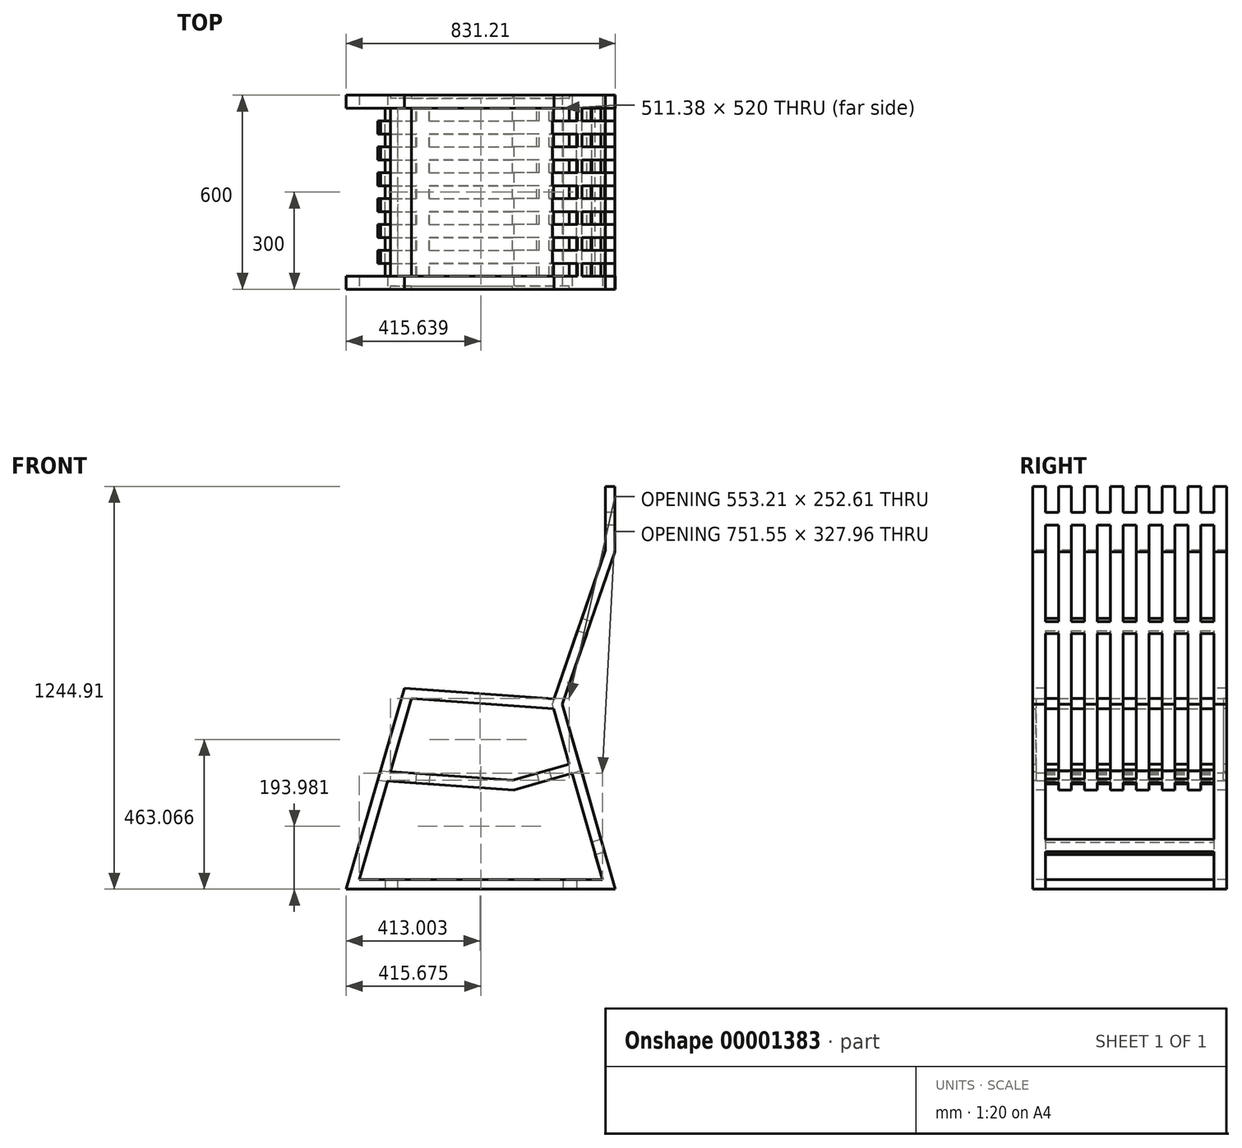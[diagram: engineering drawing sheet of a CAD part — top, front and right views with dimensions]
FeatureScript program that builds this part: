
annotation { "Feature Type Name" : "Feature", "Feature Type Description" : "" }
export const myFeature = defineFeature(function(context is Context, id is Id, definition is map)
    precondition{}
    {
        {
            var Q0;
            Q0=qCreatedBy(makeId("Front.planeOp"),FACE);
            var sketch = newSketch(context, id + "F0", { "sketchPlane" : qUnion([Q0])});
            skLineSegment(sketch, "E0", {"start": v(0, 0) * mm, "end": v(175.03, 605.2) * mm, "construction": true});
            skLineSegment(sketch, "E1", {"start": v(101.23, 350) * mm, "end": v(500.22, 321.6) * mm, "construction": true});
            skLineSegment(sketch, "E2", {"start": v(500.22, 321.6) * mm, "end": v(692.54, 376.5) * mm, "construction": true});
            skLineSegment(sketch, "E3", {"start": v(692.54, 376.5) * mm, "end": v(636.64, 572.35) * mm, "construction": true});
            skLineSegment(sketch, "E4", {"start": v(636.64, 572.35) * mm, "end": v(800, 1044.91) * mm, "construction": true});
            skLineSegment(sketch, "E5", {"start": v(0, 0) * mm, "end": v(800, 0) * mm, "construction": true});
            skLineSegment(sketch, "E6", {"start": v(800, 1044.91) * mm, "end": v(800, 1244.91) * mm, "construction": true});
            skLineSegment(sketch, "E7", {"start": v(636.64, 572.35) * mm, "end": v(175.03, 605.2) * mm, "construction": true});
            skLineSegment(sketch, "E8", {"start": v(815.6, 0) * mm, "end": v(-15.61, 0) * mm});
            skLineSegment(sketch, "E9", {"start": v(800, 1244.91) * mm, "end": v(800, 1044.91) * mm});
            skLineSegment(sketch, "E10.0", {"start": v(785, 1244.91) * mm, "end": v(785, 1044.91) * mm});
            skLineSegment(sketch, "E11.0", {"start": v(815, 1244.91) * mm, "end": v(815, 1044.91) * mm});
            skLineSegment(sketch, "E12.0", {"start": v(785.82, 1049.81) * mm, "end": v(626.22, 588.13) * mm});
            skLineSegment(sketch, "E13.0", {"start": v(815, 1042.4) * mm, "end": v(652.36, 571.92) * mm});
            skLineSegment(sketch, "E13.1", {"start": v(815, 1244.91) * mm, "end": v(815, 1042.4) * mm});
            skLineSegment(sketch, "E14.0", {"start": v(164, 621.02) * mm, "end": v(-15.61, 0) * mm});
            skLineSegment(sketch, "E14.2", {"start": v(815.6, 0) * mm, "end": v(652.36, 571.92) * mm});
            skLineSegment(sketch, "E15.0", {"start": v(682.23, 357.96) * mm, "end": v(501.8, 306.46) * mm});
            skLineSegment(sketch, "E15.1", {"start": v(112.27, 334.18) * mm, "end": v(501.8, 306.46) * mm});
            skLineSegment(sketch, "E16.0", {"start": v(674, 386.8) * mm, "end": v(498.64, 336.76) * mm});
            skLineSegment(sketch, "E16.1", {"start": v(120.79, 363.65) * mm, "end": v(498.64, 336.76) * mm});
            skLineSegment(sketch, "E17.0", {"start": v(775.84, 30) * mm, "end": v(682.23, 357.96) * mm});
            skLineSegment(sketch, "E17.2", {"start": v(186.07, 589.37) * mm, "end": v(120.79, 363.65) * mm});
            skLineSegment(sketch, "E17.3", {"start": v(186.07, 589.37) * mm, "end": v(625.1, 558.13) * mm});
            skLineSegment(sketch, "E18.0", {"start": v(775.84, 30) * mm, "end": v(24.3, 30) * mm});
            skLineSegment(sketch, "E19", {"start": v(785, 1244.91) * mm, "end": v(815, 1244.91) * mm});
            skLineSegment(sketch, "E20", {"start": v(164, 621.02) * mm, "end": v(626.22, 588.13) * mm});
            skLineSegment(sketch, "E21.trimOffspring", {"start": v(112.27, 334.18) * mm, "end": v(24.3, 30) * mm});
            skLineSegment(sketch, "E22.trimOffspring", {"start": v(674, 386.8) * mm, "end": v(625.1, 558.13) * mm});
            skSolve(sketch);
        }
        {
            var Q0;
            Q0 = qSketchRegion(id + "F0", true);
            extrude(context, id + "F1", {"entities" : qUnion([Q0]), "oppositeDirection" : true, "depth" : 30 * mm});
        }
        {
            var Q0;
            Q0=makeQuery(id+"F1.opExtrude","CAP_FACE",FACE,{"disambiguationData":[OSD([sQuery(id+"F0.wireOp",EDGE,"E8"),sQuery(id+"F0.wireOp",EDGE,"E10.0"),sQuery(id+"F0.wireOp",EDGE,"E12.0"),sQuery(id+"F0.wireOp",EDGE,"E13.0"),sQuery(id+"F0.wireOp",EDGE,"E13.1"),sQuery(id+"F0.wireOp",EDGE,"E14.0"),sQuery(id+"F0.wireOp",EDGE,"E14.2"),sQuery(id+"F0.wireOp",EDGE,"E15.0"),sQuery(id+"F0.wireOp",EDGE,"E15.1"),sQuery(id+"F0.wireOp",EDGE,"E16.0"),sQuery(id+"F0.wireOp",EDGE,"E16.1"),sQuery(id+"F0.wireOp",EDGE,"E17.0"),sQuery(id+"F0.wireOp",EDGE,"E17.2"),sQuery(id+"F0.wireOp",EDGE,"E17.3"),sQuery(id+"F0.wireOp",EDGE,"E18.0"),sQuery(id+"F0.wireOp",EDGE,"E19"),sQuery(id+"F0.wireOp",EDGE,"E20"),sQuery(id+"F0.wireOp",EDGE,"E21.trimOffspring"),sQuery(id+"F0.wireOp",EDGE,"E22.trimOffspring")])],"isStart":false});
            var sketch = newSketch(context, id + "F2", { "sketchPlane" : qUnion([Q0])});
            skLineSegment(sketch, "E23.2", {"start": v(-90.19, 365.82) * mm, "end": v(-81.67, 336.35) * mm});
            skLineSegment(sketch, "E24", {"start": v(-652.36, 571.92) * mm, "end": v(-711.08, 366.2) * mm});
            skLineSegment(sketch, "E25", {"start": v(-785, 1244.91) * mm, "end": v(-815, 1244.91) * mm});
            skLineSegment(sketch, "E26", {"start": v(-815, 1244.91) * mm, "end": v(-815, 1042.4) * mm});
            skLineSegment(sketch, "E27", {"start": v(-815, 1042.4) * mm, "end": v(-652.36, 571.92) * mm});
            skLineSegment(sketch, "E28", {"start": v(-785, 1244.91) * mm, "end": v(-785, 1047.43) * mm});
            skLineSegment(sketch, "E29", {"start": v(-785, 1047.43) * mm, "end": v(-626.22, 588.13) * mm});
            skLineSegment(sketch, "E30", {"start": v(-620.92, 572.78) * mm, "end": v(-674, 386.8) * mm});
            skLineSegment(sketch, "E31", {"start": v(-674, 386.8) * mm, "end": v(-498.64, 336.76) * mm});
            skLineSegment(sketch, "E32", {"start": v(-498.64, 336.76) * mm, "end": v(-90.19, 365.82) * mm});
            skLineSegment(sketch, "E33", {"start": v(-711.08, 366.2) * mm, "end": v(-501.8, 306.46) * mm});
            skLineSegment(sketch, "E34", {"start": v(-501.8, 306.46) * mm, "end": v(-81.67, 336.35) * mm});
            skPoint(sketch, "E35.orphan", {"position": v(-164, 621.02) * mm});
            skPoint(sketch, "E36.orphan", {"position": v(15.61, 0) * mm});
            skLineSegment(sketch, "E37", {"start": v(-620.92, 572.78) * mm, "end": v(-626.22, 588.13) * mm});
            skSolve(sketch);
        }
        {
            var Q0;
            {var subQ2=sQuery(id+"F2.wireOp",EDGE,"E23.2");Q0=makeQuery(id+"F2.imprint","IMPRINT",FACE,{"disambiguationData":[TD([[makeQuery(id+"F2.imprint","IMPRINT",EDGE,{"derivedFrom":subQ2}),-1.0]])]});}
            extrude(context, id + "F3", {"entities" : qUnion([Q0]), "operationType" : NewBodyOperationType.ADD, "depth" : 520 * mm});
        }
        {
            var Q0;
            Q0=makeQuery(id+"F3.opExtrude","CAP_FACE",FACE,{"disambiguationData":[OSD([sQuery(id+"F2.wireOp",EDGE,"E23.2"),sQuery(id+"F2.wireOp",EDGE,"E24"),sQuery(id+"F2.wireOp",EDGE,"E25"),sQuery(id+"F2.wireOp",EDGE,"E26"),sQuery(id+"F2.wireOp",EDGE,"E27"),sQuery(id+"F2.wireOp",EDGE,"E28"),sQuery(id+"F2.wireOp",EDGE,"E29"),sQuery(id+"F2.wireOp",EDGE,"E30"),sQuery(id+"F2.wireOp",EDGE,"E31"),sQuery(id+"F2.wireOp",EDGE,"E32"),sQuery(id+"F2.wireOp",EDGE,"E33"),sQuery(id+"F2.wireOp",EDGE,"E34"),sQuery(id+"F2.wireOp",EDGE,"E37")])],"isStart":false});
            var sketch = newSketch(context, id + "F4", { "sketchPlane" : qUnion([Q0])});
            skLineSegment(sketch, "E38", {"start": v(-785, 1244.91) * mm, "end": v(-815, 1244.91) * mm});
            skLineSegment(sketch, "E39", {"start": v(-815, 1244.91) * mm, "end": v(-815, 1042.4) * mm});
            skLineSegment(sketch, "E40", {"start": v(-815, 1042.4) * mm, "end": v(-652.36, 571.92) * mm});
            skLineSegment(sketch, "E41", {"start": v(-652.36, 571.92) * mm, "end": v(-815.6, 0) * mm});
            skLineSegment(sketch, "E42", {"start": v(-785, 1244.91) * mm, "end": v(-785, 1047.43) * mm});
            skLineSegment(sketch, "E43", {"start": v(-785, 1047.43) * mm, "end": v(-626.22, 588.13) * mm});
            skLineSegment(sketch, "E44", {"start": v(-625.1, 558.13) * mm, "end": v(-674, 386.8) * mm});
            skLineSegment(sketch, "E45", {"start": v(-674, 386.8) * mm, "end": v(-498.64, 336.76) * mm});
            skLineSegment(sketch, "E46", {"start": v(-498.64, 336.76) * mm, "end": v(-120.79, 363.65) * mm});
            skLineSegment(sketch, "E47.0", {"start": v(-164, 621.02) * mm, "end": v(15.61, 0) * mm});
            skLineSegment(sketch, "E48.0", {"start": v(-164, 621.02) * mm, "end": v(-626.22, 588.13) * mm});
            skLineSegment(sketch, "E49.0", {"start": v(-186.07, 589.37) * mm, "end": v(-120.79, 363.65) * mm});
            skLineSegment(sketch, "E50.0", {"start": v(-186.07, 589.37) * mm, "end": v(-625.1, 558.13) * mm});
            skLineSegment(sketch, "E51.0", {"start": v(-112.27, 334.18) * mm, "end": v(-501.8, 306.46) * mm});
            skLineSegment(sketch, "E52.0", {"start": v(-682.23, 357.96) * mm, "end": v(-501.8, 306.46) * mm});
            skLineSegment(sketch, "E53.0", {"start": v(-775.84, 30) * mm, "end": v(-682.23, 357.96) * mm});
            skLineSegment(sketch, "E54.0", {"start": v(-775.84, 30) * mm, "end": v(-24.3, 30) * mm});
            skLineSegment(sketch, "E55.0", {"start": v(-112.27, 334.18) * mm, "end": v(-24.3, 30) * mm});
            skLineSegment(sketch, "E56.0", {"start": v(-815.6, 0) * mm, "end": v(15.61, 0) * mm});
            skPoint(sketch, "E57.orphan", {"position": v(-81.67, 336.35) * mm});
            skPoint(sketch, "E58.orphan", {"position": v(-711.08, 366.2) * mm});
            skSolve(sketch);
        }
        {
            var Q0;
            {var subQ8=sQuery(id+"F4.wireOp",EDGE,"E48.0");Q0=makeQuery(id+"F4.imprint","IMPRINT",FACE,{"disambiguationData":[TD([[makeQuery(id+"F4.imprint","IMPRINT",EDGE,{"derivedFrom":subQ8}),1.0]])]});}
            var Q1;
            Q1=makeQuery(id+"F4.imprint","IMPRINT",FACE,{"disambiguationData":[TD([[makeQuery(id+"F4.imprint","IMPRINT",EDGE,{"derivedFrom":sQuery(id+"F4.wireOp",EDGE,"E38")}),1.0]])]});
            var Q2;
            {var subQ1=sQuery(id+"F4.wireOp",EDGE,"E53.0");Q2=makeQuery(id+"F4.imprint","IMPRINT",FACE,{"disambiguationData":[TD([[makeQuery(id+"F4.imprint","IMPRINT",EDGE,{"derivedFrom":subQ1}),1.0]])]});}
            extrude(context, id + "F5", {"entities" : qUnion([Q0, Q1, Q2]), "operationType" : NewBodyOperationType.ADD, "depth" : 30 * mm});
        }
        {
            var Q0;
            Q0=qCreatedBy(makeId("Right.planeOp"),FACE);
            var sketch = newSketch(context, id + "F6", { "sketchPlane" : qUnion([Q0])});
            skPoint(sketch, "E59.0", {"position": v(550, 621.02) * mm});
            skLineSegment(sketch, "E60.0", {"start": v(550, 1244.91) * mm, "end": v(550, 365.82) * mm, "construction": true});
            skLineSegment(sketch, "E61.0", {"start": v(30, 621.02) * mm, "end": v(30, 365.82) * mm, "construction": true});
            skLineSegment(sketch, "E62.0", {"start": v(510, 1244.91) * mm, "end": v(510, 279.99) * mm, "construction": true});
            skLineSegment(sketch, "E63.0", {"start": v(580, 1244.91) * mm, "end": v(0, 1244.91) * mm, "construction": true});
            skLineSegment(sketch, "E64.bottom", {"start": v(550, 1244.91) * mm, "end": v(510, 1244.91) * mm});
            skLineSegment(sketch, "E64.top", {"start": v(550, 279.99) * mm, "end": v(510, 279.99) * mm});
            skLineSegment(sketch, "E64.left", {"start": v(550, 1244.91) * mm, "end": v(550, 279.99) * mm});
            skLineSegment(sketch, "E64.right", {"start": v(510, 1244.91) * mm, "end": v(510, 279.99) * mm});
            skLineSegment(sketch, "E65.0", {"start": v(470, 1244.91) * mm, "end": v(470, 279.99) * mm});
            skLineSegment(sketch, "E66.0", {"start": v(430, 1244.91) * mm, "end": v(430, 279.99) * mm});
            skLineSegment(sketch, "E67.0", {"start": v(390, 1244.91) * mm, "end": v(390, 279.99) * mm});
            skLineSegment(sketch, "E68.0", {"start": v(350, 1244.91) * mm, "end": v(350, 279.99) * mm});
            skLineSegment(sketch, "E69.0", {"start": v(310, 1244.91) * mm, "end": v(310, 279.99) * mm});
            skLineSegment(sketch, "E70.0", {"start": v(270, 1244.91) * mm, "end": v(270, 279.99) * mm});
            skLineSegment(sketch, "E71.0", {"start": v(230, 1244.91) * mm, "end": v(230, 279.99) * mm});
            skLineSegment(sketch, "E72.0", {"start": v(190, 1244.91) * mm, "end": v(190, 279.99) * mm});
            skLineSegment(sketch, "E73.0", {"start": v(150, 1244.91) * mm, "end": v(150, 279.99) * mm});
            skLineSegment(sketch, "E74.0", {"start": v(110, 1244.91) * mm, "end": v(110, 279.99) * mm});
            skLineSegment(sketch, "E75.0", {"start": v(70, 1244.91) * mm, "end": v(70, 279.99) * mm});
            skLineSegment(sketch, "E76.0", {"start": v(30, 1244.91) * mm, "end": v(30, 279.99) * mm});
            skLineSegment(sketch, "E77", {"start": v(470, 279.99) * mm, "end": v(430, 279.99) * mm});
            skLineSegment(sketch, "E78", {"start": v(390, 279.99) * mm, "end": v(350, 279.99) * mm});
            skLineSegment(sketch, "E79", {"start": v(310, 279.99) * mm, "end": v(270, 279.99) * mm});
            skLineSegment(sketch, "E80", {"start": v(230, 279.99) * mm, "end": v(190, 279.99) * mm});
            skLineSegment(sketch, "E81", {"start": v(150, 279.99) * mm, "end": v(110, 279.99) * mm});
            skLineSegment(sketch, "E82", {"start": v(70, 279.99) * mm, "end": v(30, 279.99) * mm});
            skLineSegment(sketch, "E83", {"start": v(470, 1244.91) * mm, "end": v(430, 1244.91) * mm});
            skLineSegment(sketch, "E84", {"start": v(390, 1244.91) * mm, "end": v(350, 1244.91) * mm});
            skLineSegment(sketch, "E85", {"start": v(310, 1244.91) * mm, "end": v(270, 1244.91) * mm});
            skLineSegment(sketch, "E86", {"start": v(230, 1244.91) * mm, "end": v(190, 1244.91) * mm});
            skLineSegment(sketch, "E87", {"start": v(150, 1244.91) * mm, "end": v(110, 1244.91) * mm});
            skLineSegment(sketch, "E88", {"start": v(70, 1244.91) * mm, "end": v(30, 1244.91) * mm});
            skSolve(sketch);
        }
        {
            var Q0;
            {Q0=qUnion([makeQuery(id+"F6.imprint","IMPRINT",FACE,{"disambiguationData":[TD([[makeQuery(id+"F6.imprint","IMPRINT",EDGE,{"derivedFrom":sQuery(id+"F6.wireOp",EDGE,"E64.bottom")}),1.0]])]}),makeQuery(id+"F6.imprint","IMPRINT",FACE,{"disambiguationData":[TD([[makeQuery(id+"F6.imprint","IMPRINT",EDGE,{"derivedFrom":sQuery(id+"F6.wireOp",EDGE,"E65.0")}),-1.0]])]}),makeQuery(id+"F6.imprint","IMPRINT",FACE,{"disambiguationData":[TD([[makeQuery(id+"F6.imprint","IMPRINT",EDGE,{"derivedFrom":sQuery(id+"F6.wireOp",EDGE,"E67.0")}),-1.0]])]}),makeQuery(id+"F6.imprint","IMPRINT",FACE,{"disambiguationData":[TD([[makeQuery(id+"F6.imprint","IMPRINT",EDGE,{"derivedFrom":sQuery(id+"F6.wireOp",EDGE,"E69.0")}),-1.0]])]}),makeQuery(id+"F6.imprint","IMPRINT",FACE,{"disambiguationData":[TD([[makeQuery(id+"F6.imprint","IMPRINT",EDGE,{"derivedFrom":sQuery(id+"F6.wireOp",EDGE,"E71.0")}),-1.0]])]}),makeQuery(id+"F6.imprint","IMPRINT",FACE,{"disambiguationData":[TD([[makeQuery(id+"F6.imprint","IMPRINT",EDGE,{"derivedFrom":sQuery(id+"F6.wireOp",EDGE,"E73.0")}),-1.0]])]}),makeQuery(id+"F6.imprint","IMPRINT",FACE,{"disambiguationData":[TD([[makeQuery(id+"F6.imprint","IMPRINT",EDGE,{"derivedFrom":sQuery(id+"F6.wireOp",EDGE,"E75.0")}),-1.0]])]})]);}
            extrude(context, id + "F7", {"entities" : qUnion([Q0]), "operationType" : NewBodyOperationType.REMOVE, "depth" : 1000 * mm});
        }
        {
            var Q0;
            Q0=makeQuery(id+"F5.opExtrude","CAP_FACE",FACE,{"disambiguationData":[OSD([sQuery(id+"F4.wireOp",EDGE,"E38"),sQuery(id+"F4.wireOp",EDGE,"E39"),sQuery(id+"F4.wireOp",EDGE,"E40"),sQuery(id+"F4.wireOp",EDGE,"E41"),sQuery(id+"F4.wireOp",EDGE,"E42"),sQuery(id+"F4.wireOp",EDGE,"E43"),sQuery(id+"F4.wireOp",EDGE,"E44"),sQuery(id+"F4.wireOp",EDGE,"E45"),sQuery(id+"F4.wireOp",EDGE,"E46"),sQuery(id+"F4.wireOp",EDGE,"E47.0"),sQuery(id+"F4.wireOp",EDGE,"E48.0"),sQuery(id+"F4.wireOp",EDGE,"E49.0"),sQuery(id+"F4.wireOp",EDGE,"E50.0"),sQuery(id+"F4.wireOp",EDGE,"E51.0"),sQuery(id+"F4.wireOp",EDGE,"E52.0"),sQuery(id+"F4.wireOp",EDGE,"E53.0"),sQuery(id+"F4.wireOp",EDGE,"E54.0"),sQuery(id+"F4.wireOp",EDGE,"E55.0"),sQuery(id+"F4.wireOp",EDGE,"E56.0")])],"isStart":false});
            var sketch = newSketch(context, id + "F8", { "sketchPlane" : qUnion([Q0])});
            skLineSegment(sketch, "E89.0", {"start": v(-636.64, 572.35) * mm, "end": v(-175.03, 605.2) * mm, "construction": true});
            skLineSegment(sketch, "E90.0", {"start": v(-101.23, 350) * mm, "end": v(-500.22, 321.6) * mm, "construction": true});
            skLineSegment(sketch, "E91.0", {"start": v(-500.22, 321.6) * mm, "end": v(-692.54, 376.5) * mm, "construction": true});
            skLineSegment(sketch, "E92.0", {"start": v(-795.72, 15) * mm, "end": v(-636.64, 572.35) * mm, "construction": true});
            skLineSegment(sketch, "E93.0", {"start": v(-800, 1244.91) * mm, "end": v(-800, 1044.91) * mm, "construction": true});
            skLineSegment(sketch, "E94.0", {"start": v(-636.64, 572.35) * mm, "end": v(-800, 1044.91) * mm, "construction": true});
            skLineSegment(sketch, "E95.0", {"start": v(-4.34, 15) * mm, "end": v(-175.03, 605.2) * mm, "construction": true});
            skLineSegment(sketch, "E96.0", {"start": v(-795.72, 15) * mm, "end": v(-4.34, 15) * mm, "construction": true});
            skPoint(sketch, "E97.orphan", {"position": v(0, 0) * mm});
            skPoint(sketch, "E98.orphan", {"position": v(-692.54, 376.5) * mm});
            skLineSegment(sketch, "E99.rect.bottom", {"start": v(-785, 1124.91) * mm, "end": v(-815, 1124.91) * mm});
            skLineSegment(sketch, "E99.rect.top", {"start": v(-785, 1164.91) * mm, "end": v(-815, 1164.91) * mm});
            skLineSegment(sketch, "E99.rect.left", {"start": v(-785, 1124.91) * mm, "end": v(-785, 1164.91) * mm});
            skLineSegment(sketch, "E99.rect.right", {"start": v(-815, 1124.91) * mm, "end": v(-815, 1164.91) * mm});
            skPoint(sketch, "E99.rect.middle", {"position": v(-800, 1144.91) * mm});
            skLineSegment(sketch, "E100", {"start": v(-650.16, 470.3) * mm, "end": v(-655.65, 451.08) * mm});
            skLineSegment(sketch, "E101", {"start": v(-655.65, 451.08) * mm, "end": v(-684.5, 459.31) * mm});
            skLineSegment(sketch, "E102", {"start": v(-684.5, 459.31) * mm, "end": v(-673.52, 497.78) * mm});
            skLineSegment(sketch, "E103", {"start": v(-673.52, 497.78) * mm, "end": v(-644.67, 489.54) * mm});
            skLineSegment(sketch, "E104", {"start": v(-644.67, 489.54) * mm, "end": v(-650.16, 470.3) * mm});
            skPoint(sketch, "E105.start.orphan", {"position": v(-664.59, 474.43) * mm});
            skLineSegment(sketch, "E106", {"start": v(-596.38, 349.06) * mm, "end": v(-592.26, 363.48) * mm, "construction": true});
            skLineSegment(sketch, "E107", {"start": v(-592.26, 363.48) * mm, "end": v(-611.5, 368.97) * mm});
            skLineSegment(sketch, "E108", {"start": v(-611.5, 368.97) * mm, "end": v(-619.73, 340.12) * mm});
            skLineSegment(sketch, "E109", {"start": v(-619.73, 340.12) * mm, "end": v(-581.26, 329.14) * mm});
            skLineSegment(sketch, "E110", {"start": v(-581.26, 329.14) * mm, "end": v(-573.03, 358) * mm});
            skLineSegment(sketch, "E111", {"start": v(-573.03, 358) * mm, "end": v(-592.26, 363.48) * mm});
            skLineSegment(sketch, "E112", {"start": v(-795.72, 15) * mm, "end": v(-768.27, 111.16) * mm, "construction": true});
            skLineSegment(sketch, "E113", {"start": v(-768.27, 111.16) * mm, "end": v(-753.85, 107.04) * mm});
            skLineSegment(sketch, "E114", {"start": v(-753.85, 107.04) * mm, "end": v(-742.87, 145.5) * mm});
            skLineSegment(sketch, "E115", {"start": v(-742.87, 145.5) * mm, "end": v(-771.72, 153.74) * mm});
            skLineSegment(sketch, "E116", {"start": v(-771.72, 153.74) * mm, "end": v(-782.7, 115.28) * mm});
            skLineSegment(sketch, "E117", {"start": v(-782.7, 115.28) * mm, "end": v(-768.27, 111.16) * mm});
            skLineSegment(sketch, "E118", {"start": v(-101.23, 350) * mm, "end": v(-200.97, 342.9) * mm, "construction": true});
            skLineSegment(sketch, "E119", {"start": v(-200.97, 342.9) * mm, "end": v(-199.91, 327.94) * mm});
            skLineSegment(sketch, "E120", {"start": v(-199.91, 327.94) * mm, "end": v(-239.8, 325.1) * mm});
            skLineSegment(sketch, "E121", {"start": v(-239.8, 325.1) * mm, "end": v(-241.94, 355.03) * mm});
            skLineSegment(sketch, "E122", {"start": v(-241.94, 355.03) * mm, "end": v(-202.04, 357.86) * mm});
            skLineSegment(sketch, "E123", {"start": v(-202.04, 357.86) * mm, "end": v(-200.97, 342.9) * mm});
            skLineSegment(sketch, "E124", {"start": v(-795.72, 15) * mm, "end": v(-695.72, 15) * mm, "construction": true});
            skLineSegment(sketch, "E125", {"start": v(-695.72, 15) * mm, "end": v(-695.72, 30) * mm});
            skLineSegment(sketch, "E126", {"start": v(-695.72, 30) * mm, "end": v(-655.72, 30) * mm});
            skLineSegment(sketch, "E127", {"start": v(-655.72, 30) * mm, "end": v(-655.72, 0) * mm});
            skLineSegment(sketch, "E128", {"start": v(-655.72, 0) * mm, "end": v(-695.72, 0) * mm});
            skLineSegment(sketch, "E129", {"start": v(-695.72, 0) * mm, "end": v(-695.72, 15) * mm});
            skLineSegment(sketch, "E130", {"start": v(-4.34, 15) * mm, "end": v(-104.34, 15) * mm, "construction": true});
            skLineSegment(sketch, "E131", {"start": v(-104.34, 15) * mm, "end": v(-104.34, 30) * mm});
            skLineSegment(sketch, "E132", {"start": v(-104.34, 30) * mm, "end": v(-144.34, 30) * mm});
            skLineSegment(sketch, "E133", {"start": v(-144.34, 30) * mm, "end": v(-144.34, 0) * mm});
            skLineSegment(sketch, "E134", {"start": v(-144.34, 0) * mm, "end": v(-104.34, 0) * mm});
            skLineSegment(sketch, "E135", {"start": v(-104.34, 0) * mm, "end": v(-104.34, 15) * mm});
            skLineSegment(sketch, "E136", {"start": v(-800, 1044.91) * mm, "end": v(-726.49, 832.26) * mm, "construction": true});
            skLineSegment(sketch, "E137", {"start": v(-726.49, 832.26) * mm, "end": v(-740.66, 827.36) * mm});
            skLineSegment(sketch, "E138", {"start": v(-740.66, 827.36) * mm, "end": v(-727.6, 789.55) * mm});
            skLineSegment(sketch, "E139", {"start": v(-727.6, 789.55) * mm, "end": v(-699.24, 799.35) * mm});
            skLineSegment(sketch, "E140", {"start": v(-699.24, 799.35) * mm, "end": v(-712.31, 837.16) * mm});
            skLineSegment(sketch, "E141", {"start": v(-712.31, 837.16) * mm, "end": v(-726.49, 832.26) * mm});
            skSolve(sketch);
        }
        {
            var Q0;
            Q0=makeQuery(id+"F8.imprint","IMPRINT",FACE,{"disambiguationData":[TD([[makeQuery(id+"F8.imprint","IMPRINT",EDGE,{"derivedFrom":sQuery(id+"F8.wireOp",EDGE,"E99.rect.bottom")}),-1.0]])]});
            var Q1;
            Q1=makeQuery(id+"F8.imprint","IMPRINT",FACE,{"disambiguationData":[TD([[makeQuery(id+"F8.imprint","IMPRINT",EDGE,{"derivedFrom":sQuery(id+"F8.wireOp",EDGE,"E137")}),1.0]])]});
            var Q2;
            Q2=makeQuery(id+"F8.imprint","IMPRINT",FACE,{"disambiguationData":[TD([[makeQuery(id+"F8.imprint","IMPRINT",EDGE,{"derivedFrom":sQuery(id+"F8.wireOp",EDGE,"E100")}),-1.0]])]});
            var Q3;
            Q3=makeQuery(id+"F8.imprint","IMPRINT",FACE,{"disambiguationData":[TD([[makeQuery(id+"F8.imprint","IMPRINT",EDGE,{"derivedFrom":sQuery(id+"F8.wireOp",EDGE,"E107")}),-1.0]])]});
            var Q4;
            Q4=makeQuery(id+"F8.imprint","IMPRINT",FACE,{"disambiguationData":[TD([[makeQuery(id+"F8.imprint","IMPRINT",EDGE,{"derivedFrom":sQuery(id+"F8.wireOp",EDGE,"E119")}),-1.0]])]});
            var Q5;
            Q5=makeQuery(id+"F8.imprint","IMPRINT",FACE,{"disambiguationData":[TD([[makeQuery(id+"F8.imprint","IMPRINT",EDGE,{"derivedFrom":sQuery(id+"F8.wireOp",EDGE,"E113")}),1.0]])]});
            var Q6;
            Q6=makeQuery(id+"F8.imprint","IMPRINT",FACE,{"disambiguationData":[TD([[makeQuery(id+"F8.imprint","IMPRINT",EDGE,{"derivedFrom":sQuery(id+"F8.wireOp",EDGE,"E125")}),-1.0]])]});
            var Q7;
            Q7=makeQuery(id+"F8.imprint","IMPRINT",FACE,{"disambiguationData":[TD([[makeQuery(id+"F8.imprint","IMPRINT",EDGE,{"derivedFrom":sQuery(id+"F8.wireOp",EDGE,"E131")}),1.0]])]});
            extrude(context, id + "F9", {"entities" : qUnion([Q0, Q1, Q2, Q3, Q4, Q5, Q6, Q7]), "operationType" : NewBodyOperationType.ADD, "oppositeDirection" : true, "depth" : 580 * mm});
        }
        {
            var Q0;
            Q0=makeQuery(id+"F1.opExtrude","CAP_FACE",FACE,{"disambiguationData":[OSD([sQuery(id+"F0.wireOp",EDGE,"E8"),sQuery(id+"F0.wireOp",EDGE,"E10.0"),sQuery(id+"F0.wireOp",EDGE,"E12.0"),sQuery(id+"F0.wireOp",EDGE,"E13.0"),sQuery(id+"F0.wireOp",EDGE,"E13.1"),sQuery(id+"F0.wireOp",EDGE,"E14.0"),sQuery(id+"F0.wireOp",EDGE,"E14.2"),sQuery(id+"F0.wireOp",EDGE,"E15.0"),sQuery(id+"F0.wireOp",EDGE,"E15.1"),sQuery(id+"F0.wireOp",EDGE,"E16.0"),sQuery(id+"F0.wireOp",EDGE,"E16.1"),sQuery(id+"F0.wireOp",EDGE,"E17.0"),sQuery(id+"F0.wireOp",EDGE,"E17.2"),sQuery(id+"F0.wireOp",EDGE,"E17.3"),sQuery(id+"F0.wireOp",EDGE,"E18.0"),sQuery(id+"F0.wireOp",EDGE,"E19"),sQuery(id+"F0.wireOp",EDGE,"E20"),sQuery(id+"F0.wireOp",EDGE,"E21.trimOffspring"),sQuery(id+"F0.wireOp",EDGE,"E22.trimOffspring")])],"isStart":true});
            var sketch = newSketch(context, id + "F10", { "sketchPlane" : qUnion([Q0])});
            skLineSegment(sketch, "E142.1", {"start": v(164, 621.02) * mm, "end": v(626.22, 588.13) * mm});
            skLineSegment(sketch, "E142.2", {"start": v(164, 621.02) * mm, "end": v(-15.61, 0) * mm});
            skLineSegment(sketch, "E142.3", {"start": v(186.07, 589.37) * mm, "end": v(120.79, 363.65) * mm});
            skLineSegment(sketch, "E142.4", {"start": v(186.07, 589.37) * mm, "end": v(625.1, 558.13) * mm});
            skLineSegment(sketch, "E142.5", {"start": v(120.79, 363.65) * mm, "end": v(498.64, 336.76) * mm});
            skLineSegment(sketch, "E142.6", {"start": v(674, 386.8) * mm, "end": v(498.64, 336.76) * mm});
            skLineSegment(sketch, "E142.7", {"start": v(674, 386.8) * mm, "end": v(625.1, 558.13) * mm});
            skLineSegment(sketch, "E142.8", {"start": v(815.6, 0) * mm, "end": v(652.36, 571.92) * mm});
            skLineSegment(sketch, "E142.9", {"start": v(815, 1042.4) * mm, "end": v(652.36, 571.92) * mm});
            skLineSegment(sketch, "E142.10", {"start": v(785, 1047.43) * mm, "end": v(626.22, 588.13) * mm});
            skLineSegment(sketch, "E142.11", {"start": v(785, 1244.91) * mm, "end": v(785, 1047.43) * mm});
            skLineSegment(sketch, "E142.12", {"start": v(815, 1244.91) * mm, "end": v(815, 1042.4) * mm});
            skLineSegment(sketch, "E142.13", {"start": v(785, 1244.91) * mm, "end": v(815, 1244.91) * mm});
            skLineSegment(sketch, "E142.14", {"start": v(775.84, 30) * mm, "end": v(24.3, 30) * mm});
            skLineSegment(sketch, "E142.15", {"start": v(775.84, 30) * mm, "end": v(682.23, 357.96) * mm});
            skLineSegment(sketch, "E142.16", {"start": v(682.23, 357.96) * mm, "end": v(501.8, 306.46) * mm});
            skLineSegment(sketch, "E142.17", {"start": v(112.27, 334.18) * mm, "end": v(501.8, 306.46) * mm});
            skLineSegment(sketch, "E142.18", {"start": v(112.27, 334.18) * mm, "end": v(24.3, 30) * mm});
            skLineSegment(sketch, "E142.19", {"start": v(815.6, 0) * mm, "end": v(-15.61, 0) * mm});
            skSolve(sketch);
        }
        {
            var Q0;
            Q0=makeQuery(id+"F10.imprint","IMPRINT",FACE,{"disambiguationData":[TD([[makeQuery(id+"F10.imprint","IMPRINT",EDGE,{"derivedFrom":sQuery(id+"F10.wireOp",EDGE,"E142.1")}),-1.0]])]});
            extrude(context, id + "F11", {"entities" : qUnion([Q0]), "operationType" : NewBodyOperationType.ADD, "depth" : 10 * mm});
        }
        {
            var Q0;
            Q0=makeQuery(id+"F5.opExtrude","CAP_FACE",FACE,{"disambiguationData":[OSD([sQuery(id+"F4.wireOp",EDGE,"E38"),sQuery(id+"F4.wireOp",EDGE,"E39"),sQuery(id+"F4.wireOp",EDGE,"E40"),sQuery(id+"F4.wireOp",EDGE,"E41"),sQuery(id+"F4.wireOp",EDGE,"E42"),sQuery(id+"F4.wireOp",EDGE,"E43"),sQuery(id+"F4.wireOp",EDGE,"E44"),sQuery(id+"F4.wireOp",EDGE,"E45"),sQuery(id+"F4.wireOp",EDGE,"E46"),sQuery(id+"F4.wireOp",EDGE,"E47.0"),sQuery(id+"F4.wireOp",EDGE,"E48.0"),sQuery(id+"F4.wireOp",EDGE,"E49.0"),sQuery(id+"F4.wireOp",EDGE,"E50.0"),sQuery(id+"F4.wireOp",EDGE,"E51.0"),sQuery(id+"F4.wireOp",EDGE,"E52.0"),sQuery(id+"F4.wireOp",EDGE,"E53.0"),sQuery(id+"F4.wireOp",EDGE,"E54.0"),sQuery(id+"F4.wireOp",EDGE,"E55.0"),sQuery(id+"F4.wireOp",EDGE,"E56.0")])],"isStart":false});
            var sketch = newSketch(context, id + "F12", { "sketchPlane" : qUnion([Q0])});
            skPoint(sketch, "E143.0", {"position": v(-782.7, 115.28) * mm});
            skLineSegment(sketch, "E143.1", {"start": v(-815.6, 0) * mm, "end": v(-652.36, 571.92) * mm});
            skLineSegment(sketch, "E143.2", {"start": v(-775.84, 30) * mm, "end": v(-682.23, 357.96) * mm});
            skLineSegment(sketch, "E143.3", {"start": v(-682.23, 357.96) * mm, "end": v(-501.8, 306.46) * mm});
            skLineSegment(sketch, "E143.4", {"start": v(-674, 386.8) * mm, "end": v(-498.64, 336.76) * mm});
            skLineSegment(sketch, "E143.5", {"start": v(-625.1, 558.13) * mm, "end": v(-674, 386.8) * mm});
            skLineSegment(sketch, "E143.7", {"start": v(-815, 1042.4) * mm, "end": v(-652.36, 571.92) * mm});
            skLineSegment(sketch, "E143.8", {"start": v(-626.22, 588.13) * mm, "end": v(-785, 1047.43) * mm});
            skLineSegment(sketch, "E143.9", {"start": v(-164, 621.02) * mm, "end": v(-626.22, 588.13) * mm});
            skLineSegment(sketch, "E143.10", {"start": v(-186.07, 589.37) * mm, "end": v(-625.1, 558.13) * mm});
            skLineSegment(sketch, "E143.11", {"start": v(-186.07, 589.37) * mm, "end": v(-120.79, 363.65) * mm});
            skLineSegment(sketch, "E143.12", {"start": v(-164, 621.02) * mm, "end": v(15.61, 0) * mm});
            skLineSegment(sketch, "E143.13", {"start": v(-498.64, 336.76) * mm, "end": v(-120.79, 363.65) * mm});
            skLineSegment(sketch, "E143.14", {"start": v(-112.27, 334.18) * mm, "end": v(-501.8, 306.46) * mm});
            skLineSegment(sketch, "E143.15", {"start": v(-112.27, 334.18) * mm, "end": v(-24.3, 30) * mm});
            skLineSegment(sketch, "E143.16", {"start": v(-775.84, 30) * mm, "end": v(-24.3, 30) * mm});
            skLineSegment(sketch, "E143.17", {"start": v(-815.6, 0) * mm, "end": v(15.61, 0) * mm});
            skLineSegment(sketch, "E143.18", {"start": v(-785, 1244.91) * mm, "end": v(-785, 1047.43) * mm});
            skLineSegment(sketch, "E143.19", {"start": v(-815, 1244.91) * mm, "end": v(-815, 1042.4) * mm});
            skLineSegment(sketch, "E143.20", {"start": v(-785, 1244.91) * mm, "end": v(-815, 1244.91) * mm});
            skSolve(sketch);
        }
        {
            var Q0;
            Q0=makeQuery(id+"F12.imprint","IMPRINT",FACE,{"disambiguationData":[TD([[makeQuery(id+"F12.imprint","IMPRINT",EDGE,{"derivedFrom":sQuery(id+"F12.wireOp",EDGE,"E143.1")}),-1.0]])]});
            extrude(context, id + "F13", {"entities" : qUnion([Q0]), "operationType" : NewBodyOperationType.ADD, "depth" : 10 * mm});
        }
    });
